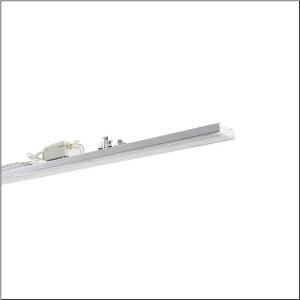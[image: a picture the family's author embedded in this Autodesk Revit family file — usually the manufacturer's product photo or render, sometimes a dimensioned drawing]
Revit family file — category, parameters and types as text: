
# Revit family: licross_21_recessed_mo_52tl12dn395g
name_source: partatom
category: Lighting Fixtures
units: mm (PartAtom-declared; Revit-internal decimal feet)

## family parameters
Cut with Voids When Loaded = No
Host = Face
Light Source = No
Part Type = Normal
Room Calculation Point = No
Round Connector Dimension = Use Diameter
Shared = No

## types (1)
- --- (1 x LED, 9630 lm, 58 W, 3000K)
    Apparent Load = 58 VA
    CIE Flux Codes = 72 92 99 100 100
    Color Rendering = 80
    Color Temperature = 3000K
    Default Elevation = 1800 mm
    Description = Licross 21 Recessed MO, luminaire insert, of sheet steel, galvanised, coil coated, white, length: 1.500mm, width: 66mm, height: 67mm, LED rated luminous flux: 9.630lm, light colour: 830, SDCM (Standard Deviation of Colour Matching)MacAdam ≤ 3 SDCM (initial), control gear: DALI 2, with plug, 5-pole, with phase selection, mains connection: 220..240V, AC, 50/60Hz, rated input power: 58W, internal wiring halogen-free, primary optical cover: cover, of PMMA, light emission: direct distribution, primary light characteristic: symmetric, protection rating (complete): IP40, insulation class (complete): insulation class I (protective earthing), certification: CE, ENEC, VDE, UKCA, protection symbol: D if used in an environment without relevant dust loads with corresponding accessories, impact resistance: IK06, permissible ambient temperature for indoor applications: -25..+35°C, corresponds to IFS (International Featured Standards) requirements for safety and quality in the food industry, reducing of maximum allowable ambient temperature of 5°C with ceiling mounting, LABS conformity tested according to VDMA 24364:2018-05, The light source and the operating device comply with the requirements of the Ecodesign Regulation (EU) 2019/2020 and are replaceable in accordance with this regulation, packaging unit: 1 piece
    Height = 58 mm
    Lamp = 1 x LED
    Lamp Light Flux = 9630 lm
    Lamp Power = 58 W
    Lamp count = 1
    Length = 1500 mm
    Luminous efficacy = 166 lm/W
    Manufacturer = Siteco
    ModVariant = No
    Model = 52TL12DN395G
    Mounting Place = Ceiling
    Mounting Type = Pendant
    Number of Poles = 1
    OnlyDefault = Yes
    Power Factor = 1
    Product Name = Licross 21 Recessed MO
    Product group = luminaire insert | ceiling pendant
    ProductGroupID = 901
    Protection Class = Protection class I
    Protection Degree = IP 40
    RLX_Detail_Level = 1
    RLX_Emergency_Light_Flux = 0 lm
    RLX_Emergency_Type = 0
    RLX_Emergency_Type_DB = No
    RlxData = <blob elided: 24829 chars, md5=c8094d42>
    Socket = socket
    Standby Power = 0 W
    System Light Flux = 9630 lm
    System Power = 58 W
    Type Comments = factory setting: luminous flux: 100 % | dim-lin: 254 | 390 mA
    Type Image = l_1296930.jpg
    URL = http://relux.com
    VarID = @adj_095101
    Voltage = 0 V
    Weight = 0.00 kg
    Width = 66 mm

## geometry (parser evidence)
native form markers: Blend x4, Sweep x13
no freeform markers — native parametric forms only
